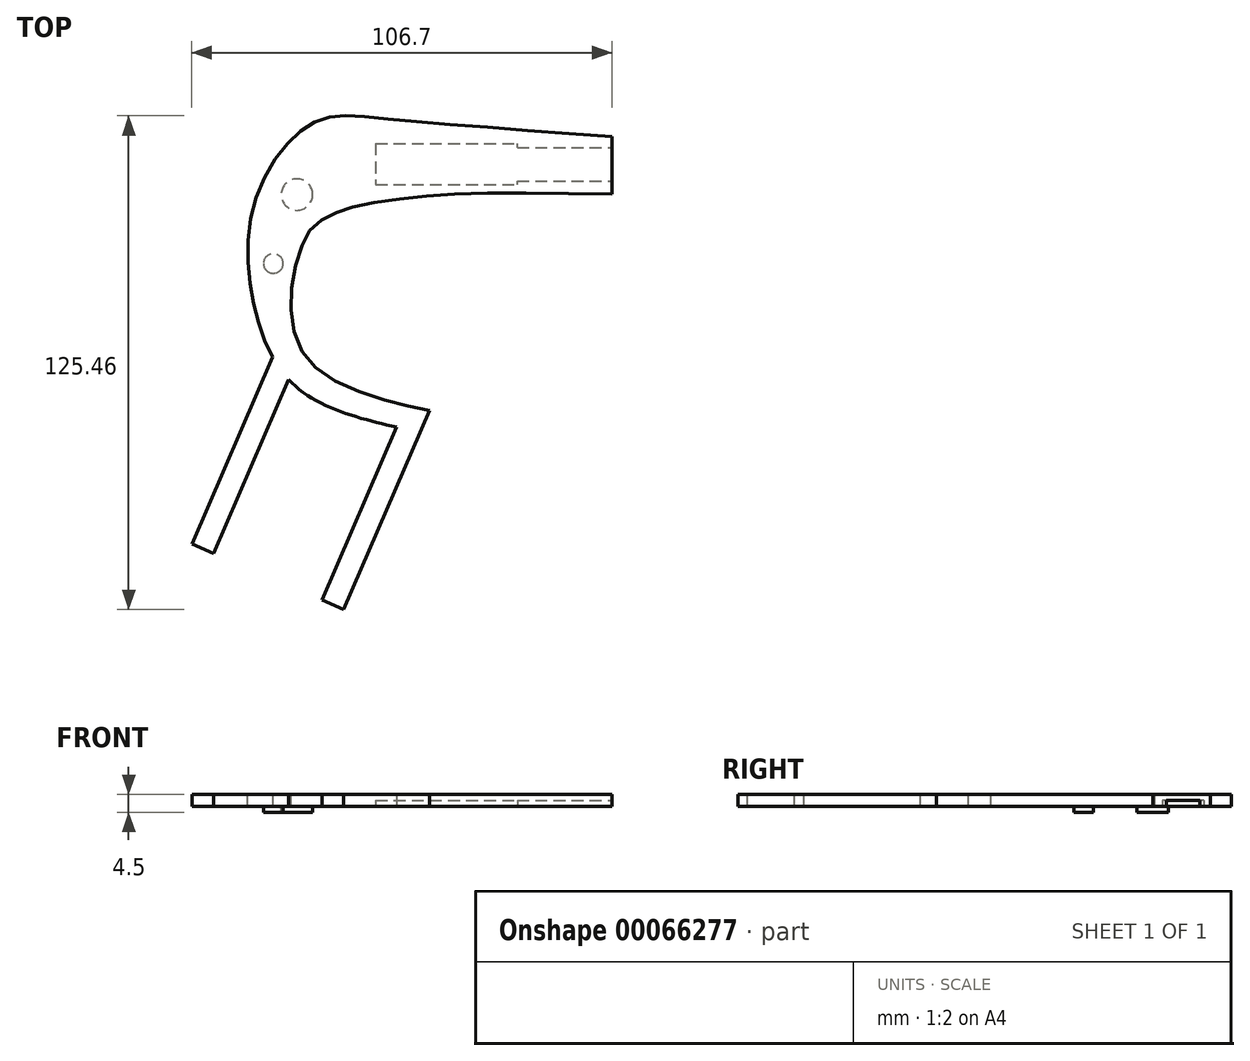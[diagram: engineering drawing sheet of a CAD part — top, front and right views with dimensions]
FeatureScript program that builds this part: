
annotation { "Feature Type Name" : "Feature", "Feature Type Description" : "" }
export const myFeature = defineFeature(function(context is Context, id is Id, definition is map)
    precondition{}
    {
        {
            var Q0;
            Q0=qCreatedBy(makeId("Top.planeOp"),FACE);
            var sketch = newSketch(context, id + "F0", { "sketchPlane" : qUnion([Q0])});
            skFitSpline(sketch, "E0", {"points": [v(-95.26, -3.24) * mm, v(-105.84, -0.7) * mm, v(-119.37, 4.45) * mm, v(-127.17, 11.15) * mm, v(-130.23, 20.05) * mm, v(-129.95, 30.26) * mm, v(-127.35, 39.49) * mm, v(-124.45, 43.95) * mm, v(-119.46, 46.88) * mm, v(-113.43, 48.8) * mm, v(-100.8, 50.8) * mm, v(-83.48, 52.02) * mm, v(-48.92, 51.78) * mm], "startDerivative": vector(-122, 25.6) * mm, "endDerivative": vector(252, -4.46) * mm});
            skLineSegment(sketch, "E1", {"start": v(-48.92, 66.37) * mm, "end": v(-48.92, 51.78) * mm});
            skFitSpline(sketch, "E2", {"points": [v(-97.6, -8.65) * mm, v(-111.92, -5.34) * mm, v(-127.2, 1.3) * mm, v(-136.04, 12.22) * mm, v(-140.54, 27.34) * mm, v(-140.42, 47.13) * mm, v(-131.94, 63.93) * mm, v(-121.94, 71.03) * mm, v(-107.3, 71.03) * mm, v(-48.92, 66.37) * mm], "startDerivative": vector(-130.63, 24.59) * mm, "endDerivative": vector(348.84, -26.12) * mm});
            skLineSegment(sketch, "E3", {"start": v(-95.26, -3.24) * mm, "end": v(-117.05, -53.74) * mm});
            skLineSegment(sketch, "E4", {"start": v(-122.56, -51.37) * mm, "end": v(-103.6, -7.43) * mm});
            skLineSegment(sketch, "E5", {"start": v(-131.03, 4.73) * mm, "end": v(-150.1, -39.48) * mm});
            skLineSegment(sketch, "E6", {"start": v(-155.62, -37.1) * mm, "end": v(-135.1, 10.43) * mm});
            skLineSegment(sketch, "E7", {"start": v(-117.05, -53.74) * mm, "end": v(-122.56, -51.37) * mm});
            skLineSegment(sketch, "E8", {"start": v(-122.56, -51.37) * mm, "end": v(-155.62, -37.1) * mm});
            skSolve(sketch);
        }
        {
            var Q0;
            {var subQ6=sQuery(id+"F0.wireOp",EDGE,"E0");Q0=makeQuery(id+"F0.imprint","IMPRINT",FACE,{"disambiguationData":[TD([[makeQuery(id+"F0.imprint","IMPRINT",EDGE,{"derivedFrom":subQ6}),1.0]])]});}
            var Q1;
            {var subQ3=sQuery(id+"F0.wireOp",EDGE,"E4");Q1=makeQuery(id+"F0.imprint","IMPRINT",FACE,{"disambiguationData":[TD([[makeQuery(id+"F0.imprint","IMPRINT",EDGE,{"derivedFrom":subQ3}),-1.0]])]});}
            var Q2;
            {var subQ0=sQuery(id+"F0.wireOp",EDGE,"E5");Q2=makeQuery(id+"F0.imprint","IMPRINT",FACE,{"disambiguationData":[TD([[makeQuery(id+"F0.imprint","IMPRINT",EDGE,{"derivedFrom":subQ0}),-1.0]])]});}
            extrude(context, id + "F1", {"entities" : qUnion([Q0, Q1, Q2]), "depth" : 3 * mm});
        }
        {
            var Q0;
            Q0=makeQuery(id+"F1.opExtrude","SWEPT_FACE",FACE,{"disambiguationData":[OSD([sQuery(id+"F0.wireOp",EDGE,"E1")])]});
            var sketch = newSketch(context, id + "F2", { "sketchPlane" : qUnion([Q0])});
            skLineSegment(sketch, "E9.bottom", {"start": v(63.67, 0) * mm, "end": v(55.17, 0) * mm});
            skLineSegment(sketch, "E9.top", {"start": v(63.67, 1.5) * mm, "end": v(55.17, 1.5) * mm});
            skLineSegment(sketch, "E9.left", {"start": v(63.67, 0) * mm, "end": v(63.67, 1.5) * mm});
            skLineSegment(sketch, "E9.right", {"start": v(55.17, 0) * mm, "end": v(55.17, 1.5) * mm});
            skSolve(sketch);
        }
        {
            var Q0;
            Q0=makeQuery(id+"F2.imprint","IMPRINT",FACE,{"disambiguationData":[TD([[makeQuery(id+"F2.imprint","IMPRINT",EDGE,{"derivedFrom":sQuery(id+"F2.wireOp",EDGE,"E9.bottom")}),-1.0]])]});
            extrude(context, id + "F3", {"entities" : qUnion([Q0]), "operationType" : NewBodyOperationType.REMOVE, "oppositeDirection" : true, "depth" : 60 * mm});
        }
        {
            var Q0;
            Q0=makeQuery(id+"F1.opExtrude","CAP_FACE",FACE,{"disambiguationData":[OSD([sQuery(id+"F0.wireOp",EDGE,"E0"),sQuery(id+"F0.wireOp",EDGE,"E1"),sQuery(id+"F0.wireOp",EDGE,"E2"),sQuery(id+"F0.wireOp",EDGE,"E3"),sQuery(id+"F0.wireOp",EDGE,"E4"),sQuery(id+"F0.wireOp",EDGE,"E5"),sQuery(id+"F0.wireOp",EDGE,"E6"),sQuery(id+"F0.wireOp",EDGE,"E7"),sQuery(id+"F0.wireOp",EDGE,"E8")])],"isStart":true});
            var sketch = newSketch(context, id + "F4", { "sketchPlane" : qUnion([Q0])});
            skLineSegment(sketch, "E10.bottom", {"start": v(-108.92, -54.17) * mm, "end": v(-72.92, -54.17) * mm});
            skLineSegment(sketch, "E10.top", {"start": v(-108.92, -64.67) * mm, "end": v(-72.92, -64.67) * mm});
            skLineSegment(sketch, "E10.left", {"start": v(-108.92, -54.17) * mm, "end": v(-108.92, -64.67) * mm});
            skLineSegment(sketch, "E10.right", {"start": v(-72.92, -54.17) * mm, "end": v(-72.92, -64.67) * mm});
            skCircle(sketch, "E11", {"center": v(-128.92, -51.67) * mm, "radius": 4 * mm});
            skCircle(sketch, "E12", {"center": v(-134.92, -34.17) * mm, "radius": 2.5 * mm});
            skSolve(sketch);
        }
        {
            var Q0;
            {var subQ0=sQuery(id+"F4.wireOp",EDGE,"E10.bottom");Q0=makeQuery(id+"F4.imprint","IMPRINT",FACE,{"disambiguationData":[TD([[makeQuery(id+"F4.imprint","IMPRINT",EDGE,{"derivedFrom":subQ0}),-1.0]])]});}
            var Q1;
            {var subQ0=sQuery(id+"F4.wireOp",EDGE,"E10.top");Q1=makeQuery(id+"F4.imprint","IMPRINT",FACE,{"disambiguationData":[TD([[makeQuery(id+"F4.imprint","IMPRINT",EDGE,{"derivedFrom":subQ0}),1.0]])]});}
            extrude(context, id + "F5", {"entities" : qUnion([Q0, Q1]), "operationType" : NewBodyOperationType.REMOVE, "oppositeDirection" : true, "depth" : 1.5 * mm});
        }
        {
            var Q0;
            Q0=makeQuery(id+"F4.imprint","IMPRINT",FACE,{"disambiguationData":[TD([[makeQuery(id+"F4.imprint","IMPRINT",EDGE,{"derivedFrom":sQuery(id+"F4.wireOp",EDGE,"E11")}),1.0]])]});
            var Q1;
            Q1=makeQuery(id+"F4.imprint","IMPRINT",FACE,{"disambiguationData":[TD([[makeQuery(id+"F4.imprint","IMPRINT",EDGE,{"derivedFrom":sQuery(id+"F4.wireOp",EDGE,"E12")}),1.0]])]});
            extrude(context, id + "F6", {"entities" : qUnion([Q0, Q1]), "operationType" : NewBodyOperationType.ADD, "depth" : 1.5 * mm});
        }
    });
